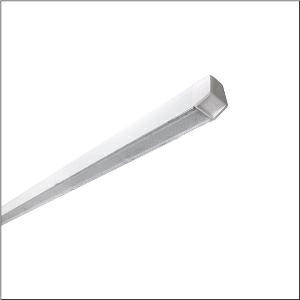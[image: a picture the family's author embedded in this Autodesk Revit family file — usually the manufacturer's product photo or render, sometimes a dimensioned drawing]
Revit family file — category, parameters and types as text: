
# Revit family: licross_r__11_recessed_mo_51ul1edv4e5f00s_da31
name_source: partatom
category: Lighting Fixtures
units: mm (PartAtom-declared; Revit-internal decimal feet)

## family parameters
Cut with Voids When Loaded = No
Host = Face
Light Source = No
Part Type = Normal
Room Calculation Point = No
Round Connector Dimension = Use Diameter
Shared = No

## types (1)
- --- (1 x LED, 14910 lm, 89.6 W, 4000K)
    Apparent Load = 90 VA
    CIE Flux Codes = 85 95 99 100 100
    Color Rendering = 80
    Color Temperature = 4000K
    Default Elevation = 1800 mm
    Description = Licross® 11 Recessed MO, single luminaire, primary optical cover: cover, of PMMA, light emission: direct distribution, primary light characteristic: symmetric, installation type: slip-in mounting, LED, rated luminous flux: 14.910lm, luminous efficacy: 166lm/W, light colour: 840, colour temperature: 4000K, control gear: ECG DALI, with terminal, 5-pole, max. 2.5mm², mains connection: 230V, AC, 50/60Hz, rated input power: 90W, Licross® LED insert, of sheet steel, galvanised, coil coated, white, with terminals, length: 2.327mm, width: 70mm, height: 71mm, end cap, of PC, white, mounting rail, of sheet steel, galvanised, white, protection rating (complete): IP20, insulation class (complete): insulation class I (protective earthing), certification: CE, ENEC, VDE, UKCA, impact resistance: IK06, permissible operating ambient temperature: -25..+35°C, corresponds to IFS (International Featured Standards) requirements for safety and quality in the food industry, reducing of maximum allowable ambient temperature of 5°C with ceiling mounting, LABS conformity tested according to VDMA 24364:2018-05, packaging unit: 1 piece
    Height = 58 mm
    Lamp = 1 x LED
    Lamp Light Flux = 14910 lm
    Lamp Power = 89.6 W
    Lamp count = 1
    Length = 2250 mm
    Luminous efficacy = 166 lm/W
    Manufacturer = Siteco
    ModVariant = No
    Model = 51UL1EDV4E5F00S
    Mounting Place = Ceiling
    Mounting Type = Pendant
    Number of Poles = 1
    OnlyDefault = Yes
    Power Factor = 1
    Product Name = Licross® 11 Recessed MO
    Product group = single luminaire
    ProductGroupID = 907
    Protection Class = Protection class I
    Protection Degree = IP 20
    RLX_Detail_Level = 1
    RLX_Emergency_Light_Flux = 0 lm
    RLX_Emergency_Type = 0
    RLX_Emergency_Type_DB = No
    RlxData = <blob elided: 32157 chars, md5=53999d93>
    Socket = socket
    Standby Power = 0 W
    System Light Flux = 14910 lm
    System Power = 90 W
    Type Comments = factory setting: luminous flux: 100 % | dim-lin: 254 | 400 mA
    Type Image = l_1006979.jpg
    URL = http://relux.com
    VarID = @adj_112523
    Voltage = 0 V
    Weight = 0.00 kg
    Width = 66 mm

## geometry (parser evidence)
native form markers: Blend x4, Sweep x10
no freeform markers — native parametric forms only
